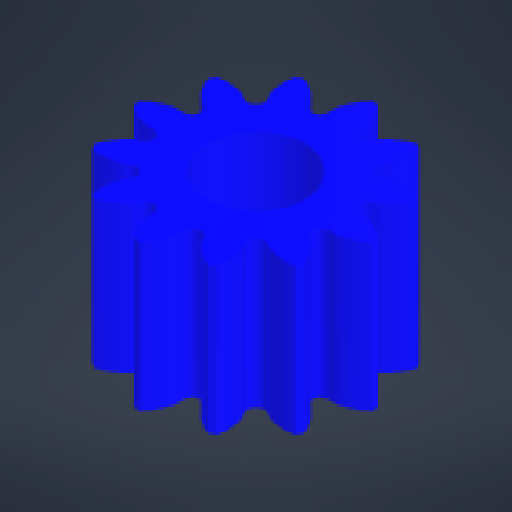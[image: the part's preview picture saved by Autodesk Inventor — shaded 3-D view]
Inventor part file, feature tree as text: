
AUTODESK INVENTOR PART (.ipt)
format: ipt  version: 2024 (Build 280153000, 153)  size: 360,960 bytes
history: native  units: mm
features: extrude x2, sketch x2, projected_geometry x2, other x1, imported_body x1
ambient origin geometry x8: Origin, YZ Plane, XZ Plane, XY Plane, X Axis, Y Axis, Z Axis, Center Point
bodies: Body1 (feature_tree)
feature tree (8):
  other  "Твердое тело1"
  extrude  "Выдавливание1"  Depth=3.0mm TaperAngle=0.0deg
  extrude  "Выдавливание2"  Depth=3.0mm TaperAngle=0.0deg
  sketch  "Эскиз1"
  projected_geometry  "Спроецированная петля1"
  sketch  "Эскиз2"
  projected_geometry  "Спроецированная петля2"
  imported_body  "БазТело1"
